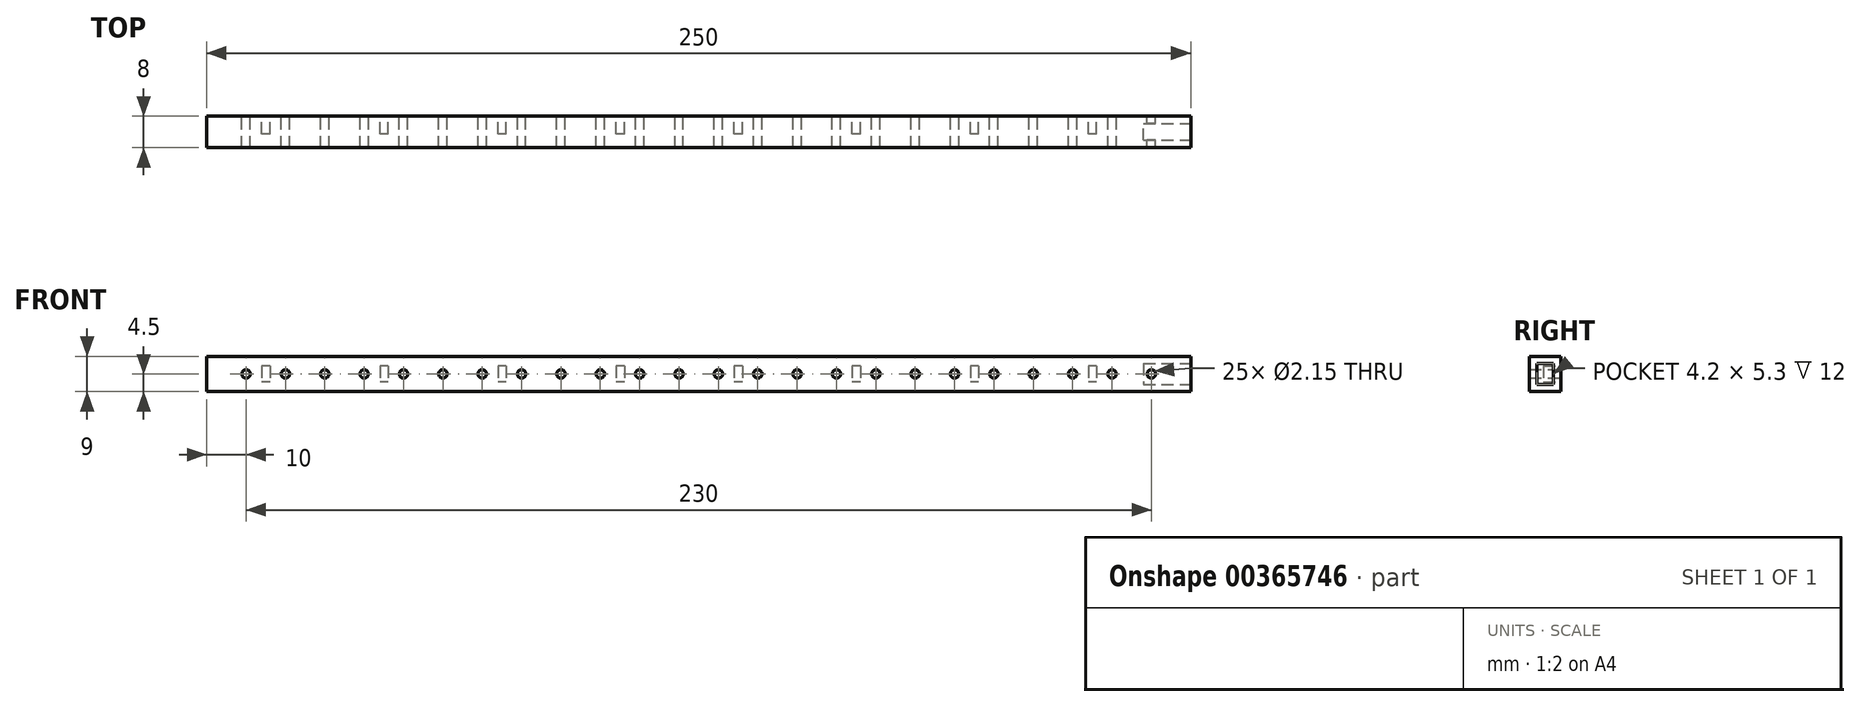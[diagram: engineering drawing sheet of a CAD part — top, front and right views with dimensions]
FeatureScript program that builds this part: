
annotation { "Feature Type Name" : "Feature", "Feature Type Description" : "" }
export const myFeature = defineFeature(function(context is Context, id is Id, definition is map)
    precondition{}
    {
        {
            var Q0;
            Q0=qCreatedBy(makeId("Front.planeOp"),FACE);
            var sketch = newSketch(context, id + "F0", { "sketchPlane" : qUnion([Q0])});
            skLineSegment(sketch, "E0.bottom", {"start": v(0, 0) * mm, "end": v(250, 0) * mm});
            skLineSegment(sketch, "E0.top", {"start": v(0, 9) * mm, "end": v(250, 9) * mm});
            skLineSegment(sketch, "E0.left", {"start": v(0, 0) * mm, "end": v(0, 9) * mm});
            skLineSegment(sketch, "E0.right", {"start": v(250, 0) * mm, "end": v(250, 9) * mm});
            skCircle(sketch, "E1", {"center": v(10, 4.5) * mm, "radius": 1.07 * mm});
            skCircle(sketch, "E2.1.0.0", {"center": v(20, 4.5) * mm, "radius": 1.07 * mm});
            skCircle(sketch, "E2.2.0.0", {"center": v(30, 4.5) * mm, "radius": 1.07 * mm});
            skCircle(sketch, "E2.3.0.0", {"center": v(40, 4.5) * mm, "radius": 1.07 * mm});
            skCircle(sketch, "E2.4.0.0", {"center": v(50, 4.5) * mm, "radius": 1.07 * mm});
            skCircle(sketch, "E2.5.0.0", {"center": v(60, 4.5) * mm, "radius": 1.07 * mm});
            skCircle(sketch, "E2.6.0.0", {"center": v(70, 4.5) * mm, "radius": 1.07 * mm});
            skCircle(sketch, "E2.7.0.0", {"center": v(80, 4.5) * mm, "radius": 1.07 * mm});
            skCircle(sketch, "E2.8.0.0", {"center": v(90, 4.5) * mm, "radius": 1.07 * mm});
            skLineSegment(sketch, "E2.direction1", {"start": v(10, 4.5) * mm, "end": v(20, 4.5) * mm, "construction": true});
            skCircle(sketch, "E3.0.9.0", {"center": v(100, 4.5) * mm, "radius": 1.07 * mm});
            skCircle(sketch, "E3.0.10.0", {"center": v(110, 4.5) * mm, "radius": 1.07 * mm});
            skCircle(sketch, "E3.0.11.0", {"center": v(120, 4.5) * mm, "radius": 1.07 * mm});
            skCircle(sketch, "E3.0.12.0", {"center": v(130, 4.5) * mm, "radius": 1.07 * mm});
            skCircle(sketch, "E3.0.13.0", {"center": v(140, 4.5) * mm, "radius": 1.07 * mm});
            skCircle(sketch, "E3.0.14.0", {"center": v(150, 4.5) * mm, "radius": 1.07 * mm});
            skCircle(sketch, "E4.0.15.0", {"center": v(160, 4.5) * mm, "radius": 1.07 * mm});
            skCircle(sketch, "E4.0.16.0", {"center": v(170, 4.5) * mm, "radius": 1.07 * mm});
            skCircle(sketch, "E4.0.17.0", {"center": v(180, 4.5) * mm, "radius": 1.07 * mm});
            skCircle(sketch, "E4.0.18.0", {"center": v(190, 4.5) * mm, "radius": 1.07 * mm});
            skCircle(sketch, "E4.0.19.0", {"center": v(200, 4.5) * mm, "radius": 1.07 * mm});
            skCircle(sketch, "E5.0.20.0", {"center": v(210, 4.5) * mm, "radius": 1.07 * mm});
            skCircle(sketch, "E5.0.21.0", {"center": v(220, 4.5) * mm, "radius": 1.07 * mm});
            skCircle(sketch, "E5.0.22.0", {"center": v(230, 4.5) * mm, "radius": 1.07 * mm});
            skCircle(sketch, "E5.0.23.0", {"center": v(240, 4.5) * mm, "radius": 1.07 * mm});
            skSolve(sketch);
        }
        {
            var Q0;
            Q0=qSketchRegion(id+"F0",true);
            extrude(context, id + "F1", {"entities" : qUnion([Q0]), "depth" : 8 * mm});
        }
        {
            var Q0;
            Q0=makeQuery(id+"F1.opExtrude","SWEPT_FACE",FACE,{"disambiguationData":[OSD([sQuery(id+"F0.wireOp",EDGE,"E0.right")])]});
            var sketch = newSketch(context, id + "F2", { "sketchPlane" : qUnion([Q0])});
            skLineSegment(sketch, "E6.bottom", {"start": v(-6.1, 7.15) * mm, "end": v(-1.9, 7.15) * mm});
            skLineSegment(sketch, "E6.top", {"start": v(-6.1, 1.85) * mm, "end": v(-1.9, 1.85) * mm});
            skLineSegment(sketch, "E6.left", {"start": v(-6.1, 7.15) * mm, "end": v(-6.1, 1.85) * mm});
            skLineSegment(sketch, "E6.right", {"start": v(-1.9, 7.15) * mm, "end": v(-1.9, 1.85) * mm});
            skSolve(sketch);
        }
        {
            var Q0;
            Q0=makeQuery(id+"F2.imprint","IMPRINT",FACE,{"disambiguationData":[TD([[makeQuery(id+"F2.imprint","IMPRINT",EDGE,{"derivedFrom":sQuery(id+"F2.wireOp",EDGE,"E6.bottom")}),-1.0]])]});
            extrude(context, id + "F3", {"entities" : qUnion([Q0]), "operationType" : NewBodyOperationType.REMOVE, "oppositeDirection" : true, "depth" : 12 * mm});
        }
        {
            var Q0;
            Q0=makeQuery(id+"F1.opExtrude","CAP_FACE",FACE,{"disambiguationData":[OSD([sQuery(id+"F0.wireOp",EDGE,"E0.bottom"),sQuery(id+"F0.wireOp",EDGE,"E0.top"),sQuery(id+"F0.wireOp",EDGE,"E0.left"),sQuery(id+"F0.wireOp",EDGE,"E0.right"),sQuery(id+"F0.wireOp",EDGE,"E1"),sQuery(id+"F0.wireOp",EDGE,"E2.1.0.0"),sQuery(id+"F0.wireOp",EDGE,"E2.2.0.0"),sQuery(id+"F0.wireOp",EDGE,"E2.3.0.0"),sQuery(id+"F0.wireOp",EDGE,"E2.4.0.0"),sQuery(id+"F0.wireOp",EDGE,"E2.5.0.0"),sQuery(id+"F0.wireOp",EDGE,"E2.6.0.0"),sQuery(id+"F0.wireOp",EDGE,"E2.7.0.0"),sQuery(id+"F0.wireOp",EDGE,"E2.8.0.0")])],"isStart":true});
            var sketch = newSketch(context, id + "F4", { "sketchPlane" : qUnion([Q0])});
            skLineSegment(sketch, "E7.bottom", {"start": v(-16.1, 6.5) * mm, "end": v(-14, 6.5) * mm});
            skLineSegment(sketch, "E7.top", {"start": v(-16.1, 2.5) * mm, "end": v(-14, 2.5) * mm});
            skLineSegment(sketch, "E7.left", {"start": v(-16.1, 6.5) * mm, "end": v(-16.1, 2.5) * mm});
            skLineSegment(sketch, "E7.right", {"start": v(-14, 6.5) * mm, "end": v(-14, 2.5) * mm});
            skLineSegment(sketch, "E8.1.0.0", {"start": v(-46.1, 6.5) * mm, "end": v(-46.1, 2.5) * mm});
            skLineSegment(sketch, "E8.1.0.1", {"start": v(-46.1, 6.5) * mm, "end": v(-44, 6.5) * mm});
            skLineSegment(sketch, "E8.1.0.2", {"start": v(-44, 6.5) * mm, "end": v(-44, 2.5) * mm});
            skLineSegment(sketch, "E8.1.0.3", {"start": v(-46.1, 2.5) * mm, "end": v(-44, 2.5) * mm});
            skLineSegment(sketch, "E8.direction1", {"start": v(-16.1, 2.5) * mm, "end": v(-46.1, 2.5) * mm, "construction": true});
            skLineSegment(sketch, "E9.0.2.0", {"start": v(-76.1, 6.5) * mm, "end": v(-76.1, 2.5) * mm});
            skLineSegment(sketch, "E9.3.2.0", {"start": v(-76.1, 6.5) * mm, "end": v(-74, 6.5) * mm});
            skLineSegment(sketch, "E9.6.2.0", {"start": v(-74, 6.5) * mm, "end": v(-74, 2.5) * mm});
            skLineSegment(sketch, "E9.9.2.0", {"start": v(-76.1, 2.5) * mm, "end": v(-74, 2.5) * mm});
            skLineSegment(sketch, "E9.0.3.0", {"start": v(-106.1, 6.5) * mm, "end": v(-106.1, 2.5) * mm});
            skLineSegment(sketch, "E9.3.3.0", {"start": v(-106.1, 6.5) * mm, "end": v(-104, 6.5) * mm});
            skLineSegment(sketch, "E9.6.3.0", {"start": v(-104, 6.5) * mm, "end": v(-104, 2.5) * mm});
            skLineSegment(sketch, "E9.9.3.0", {"start": v(-106.1, 2.5) * mm, "end": v(-104, 2.5) * mm});
            skLineSegment(sketch, "E10.0.4.0", {"start": v(-136.1, 6.5) * mm, "end": v(-136.1, 2.5) * mm});
            skLineSegment(sketch, "E10.3.4.0", {"start": v(-136.1, 6.5) * mm, "end": v(-134, 6.5) * mm});
            skLineSegment(sketch, "E10.6.4.0", {"start": v(-134, 6.5) * mm, "end": v(-134, 2.5) * mm});
            skLineSegment(sketch, "E10.9.4.0", {"start": v(-136.1, 2.5) * mm, "end": v(-134, 2.5) * mm});
            skLineSegment(sketch, "E11.0.5.0", {"start": v(-166.1, 6.5) * mm, "end": v(-166.1, 2.5) * mm});
            skLineSegment(sketch, "E11.3.5.0", {"start": v(-166.1, 6.5) * mm, "end": v(-164, 6.5) * mm});
            skLineSegment(sketch, "E11.6.5.0", {"start": v(-164, 6.5) * mm, "end": v(-164, 2.5) * mm});
            skLineSegment(sketch, "E11.9.5.0", {"start": v(-166.1, 2.5) * mm, "end": v(-164, 2.5) * mm});
            skLineSegment(sketch, "E12.0.6.0", {"start": v(-196.1, 6.5) * mm, "end": v(-196.1, 2.5) * mm});
            skLineSegment(sketch, "E12.3.6.0", {"start": v(-196.1, 6.5) * mm, "end": v(-194, 6.5) * mm});
            skLineSegment(sketch, "E12.6.6.0", {"start": v(-194, 6.5) * mm, "end": v(-194, 2.5) * mm});
            skLineSegment(sketch, "E12.9.6.0", {"start": v(-196.1, 2.5) * mm, "end": v(-194, 2.5) * mm});
            skLineSegment(sketch, "E13.0.7.0", {"start": v(-226.1, 6.5) * mm, "end": v(-226.1, 2.5) * mm});
            skLineSegment(sketch, "E13.3.7.0", {"start": v(-226.1, 6.5) * mm, "end": v(-224, 6.5) * mm});
            skLineSegment(sketch, "E13.6.7.0", {"start": v(-224, 6.5) * mm, "end": v(-224, 2.5) * mm});
            skLineSegment(sketch, "E13.9.7.0", {"start": v(-226.1, 2.5) * mm, "end": v(-224, 2.5) * mm});
            skSolve(sketch);
        }
        {
            var Q0;
            Q0=qSketchRegion(id+"F4",true);
            extrude(context, id + "F5", {"entities" : qUnion([Q0]), "operationType" : NewBodyOperationType.REMOVE, "oppositeDirection" : true, "depth" : 4.5 * mm});
        }
    });
